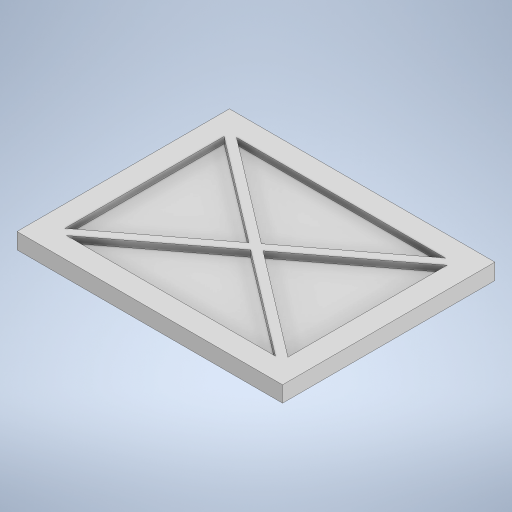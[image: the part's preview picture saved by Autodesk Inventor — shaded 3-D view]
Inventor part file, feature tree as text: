
AUTODESK INVENTOR PART (.ipt)
format: ipt  version: 2024 (Build 280153000, 153)  size: 256,000 bytes
history: native  units: mm
features: extrude x2, sketch x2, projected_geometry x1
ambient origin geometry x8: Origin, YZ Plane, XZ Plane, XY Plane, X Axis, Y Axis, Z Axis, Center Point
bodies: Solid1 (feature_tree)
feature tree (5):
  extrude  "Extrusion1"  Depth=250.0mm
  extrude  "Extrusion2"  Depth=20.0mm
  sketch  "Sketch1"  dims[d0=200.0mm d1=250.0mm]
  sketch  "Sketch2"  dims[d2=15.0mm d3=0.0mm d4=20.0mm d5=4.0mm d6=4.0mm d7=4.0mm d8=4.0mm d9=6.0mm d10=0.0mm]
  projected_geometry  "Projected Loop1"
